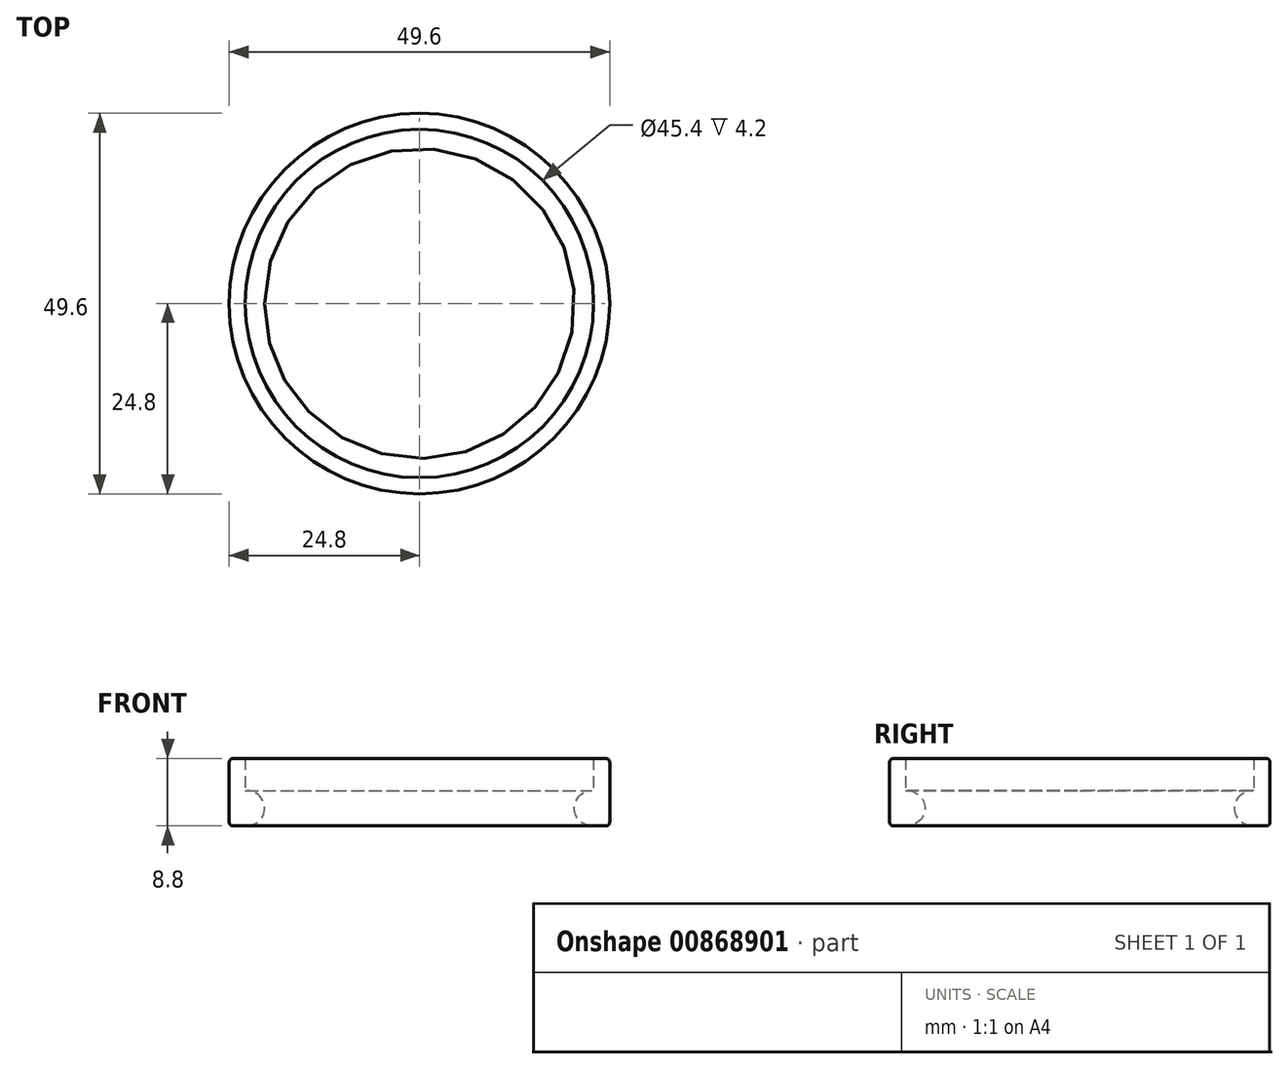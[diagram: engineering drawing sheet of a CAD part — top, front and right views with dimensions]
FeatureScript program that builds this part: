
annotation { "Feature Type Name" : "Feature", "Feature Type Description" : "" }
export const myFeature = defineFeature(function(context is Context, id is Id, definition is map)
    precondition{}
    {
        {
            var Q0;
            Q0=qCreatedBy(makeId("Top.planeOp"),FACE);
            var sketch = newSketch(context, id + "F0", { "sketchPlane" : qUnion([Q0])});
            skCircle(sketch, "E0", {"center": v(0, 0) * mm, "radius": 22.5 * mm});
            skSolve(sketch);
        }
        {
            var Q0;
            Q0=qCreatedBy(makeId("Front.planeOp"),FACE);
            var sketch = newSketch(context, id + "F1", { "sketchPlane" : qUnion([Q0])});
            skArc(sketch, "E1", {"start": v(-22.5, -2.3) * mm, "mid": v(-20.2, 0) * mm, "end": v(-22.5, 2.3) * mm});
            skLineSegment(sketch, "E2.bottom", {"start": v(-22.5, 2.3) * mm, "end": v(-22.7, 2.3) * mm});
            skLineSegment(sketch, "E2.top", {"start": v(-22.5, -2.3) * mm, "end": v(-24.3, -2.3) * mm});
            skLineSegment(sketch, "E2.right", {"start": v(-24.8, 2) * mm, "end": v(-24.8, -1.8) * mm});
            skPoint(sketch, "E3.visualSharp", {"position": v(-24.8, -2.3) * mm});
            skArc(sketch, "E3.filletArc", {"start": v(-24.8, -1.8) * mm, "mid": v(-24.65, -2.15) * mm, "end": v(-24.3, -2.3) * mm});
            skLineSegment(sketch, "E4.top", {"start": v(-24.3, 6.5) * mm, "end": v(-22.7, 6.5) * mm});
            skLineSegment(sketch, "E4.left", {"start": v(-24.8, 2) * mm, "end": v(-24.8, 6) * mm});
            skLineSegment(sketch, "E4.right", {"start": v(-22.7, 2.3) * mm, "end": v(-22.7, 6.5) * mm});
            skPoint(sketch, "E5.visualSharp", {"position": v(-24.8, 6.5) * mm});
            skArc(sketch, "E5.filletArc", {"start": v(-24.3, 6.5) * mm, "mid": v(-24.65, 6.35) * mm, "end": v(-24.8, 6) * mm});
            skSolve(sketch);
        }
        {
            var Q0;
            Q0=qSketchRegion(id+"F1",true);
            var Q1;
            Q1=sQuery(id+"F0.wireOp",EDGE,"E0");
            revolve(context, id + "F2", {"surfaceOperationType" : NewSurfaceOperationType.NEW, "entities" : qUnion([Q0]), "axis" : qUnion([Q1]), "revolveType" : RevolveType.FULL});
        }
    });
